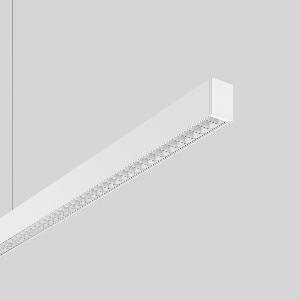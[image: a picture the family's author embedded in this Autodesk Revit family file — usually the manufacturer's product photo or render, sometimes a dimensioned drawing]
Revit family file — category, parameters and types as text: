
# Revit family: less_is_more_27_312213_002_aa41
name_source: partatom
category: Lighting Fixtures
units: mm (PartAtom-declared; Revit-internal decimal feet)

## family parameters
Cut with Voids When Loaded = No
Host = Face
Light Source = No
Part Type = Normal
Room Calculation Point = No
Round Connector Dimension = Use Diameter
Shared = No

## types (1)
- LESS IS MORE 27 (1 x LED Modul 830, 3700 lm, 3000)
    Apparent Load = 39 VA
    CIE Flux Codes = 90 99 100 64 100
    Color Rendering = 80
    Color Temperature = 3000
    Default Elevation = 1800 mm
    Description = Series: LESS IS MORE 27
Pendant luminaire with slim design. Housing: extruded aluminium profile, powder-coated. End cap aluminium powder-coated. High polish aluminium micro grid. Perfect for office areas (RUG < 19) and environments with computer screens in accordance with EN 12464-1. Direct 60%, indirect 40% light emission. Suitable for pendant. 2-point steel cable suspension, steplessly adjustable. Special lengths available on request. Converter integrated in the canopy. 
Colour: traffic white, matt (RAL 9016)
Length: 1512 mm
Width: 28 mm
Height: 38 mm
Suspension length: 100-1500 mm
Lamp: LED
Socket: without socket
Colour temperature: 3000K
Colour rendering index (CRI): 82
Light source: LED
Socket lamp2: Without base
Colour temperature: 3000K
System power: 39 W
Rated luminous flux: 3700 lm
Luminous efficiency: 95 lm/W
Control gear: Regulated power supply
Control gear: Regulated power supply
Protection class: I
Type of protection: IP 20
    Height = 38 mm
    Lamp = 1 x LED Modul 830
    Lamp Light Flux = 3700 lm
    Lamp count = 1
    Length = 1512 mm
    Lifetime = 50000 h
    Luminous efficacy = 95 lm/W
    Manufacturer = RZB
    ModVariant = No
    Model = 312213.002
    Mounting Place = Ceiling
    Mounting Type = Pendant
    Number of Poles = 1
    OnlyDefault = Yes
    Power Factor = 1
    Product Name = LESS IS MORE 27
    Product group = Pendant LED linear luminaires
    ProductGroupID = 907
    Protection Class = Protection class I
    Protection Degree = IP 20
    RLX_Detail_Level = 1
    RLX_Emergency_Light_Flux = 0 lm
    RLX_Emergency_Type = 0
    RLX_Emergency_Type_DB = No
    RlxData = <blob elided: 33469 chars, md5=14e0b235>
    Socket = socket
    Standby Power = 0 W
    System Light Flux = 3700 lm
    System Power = 39 W
    Type Comments = Product without accessories
    Type Image = 312212.002.jpg
    URL = http://relux.com
    VarID = ---
    Voltage = 230 V
    Voltage Range = 220-240 V
    Weight = 0.00 kg
    Width = 28 mm

## geometry (parser evidence)
native form markers: Blend x4, Sweep x14
no freeform markers — native parametric forms only
